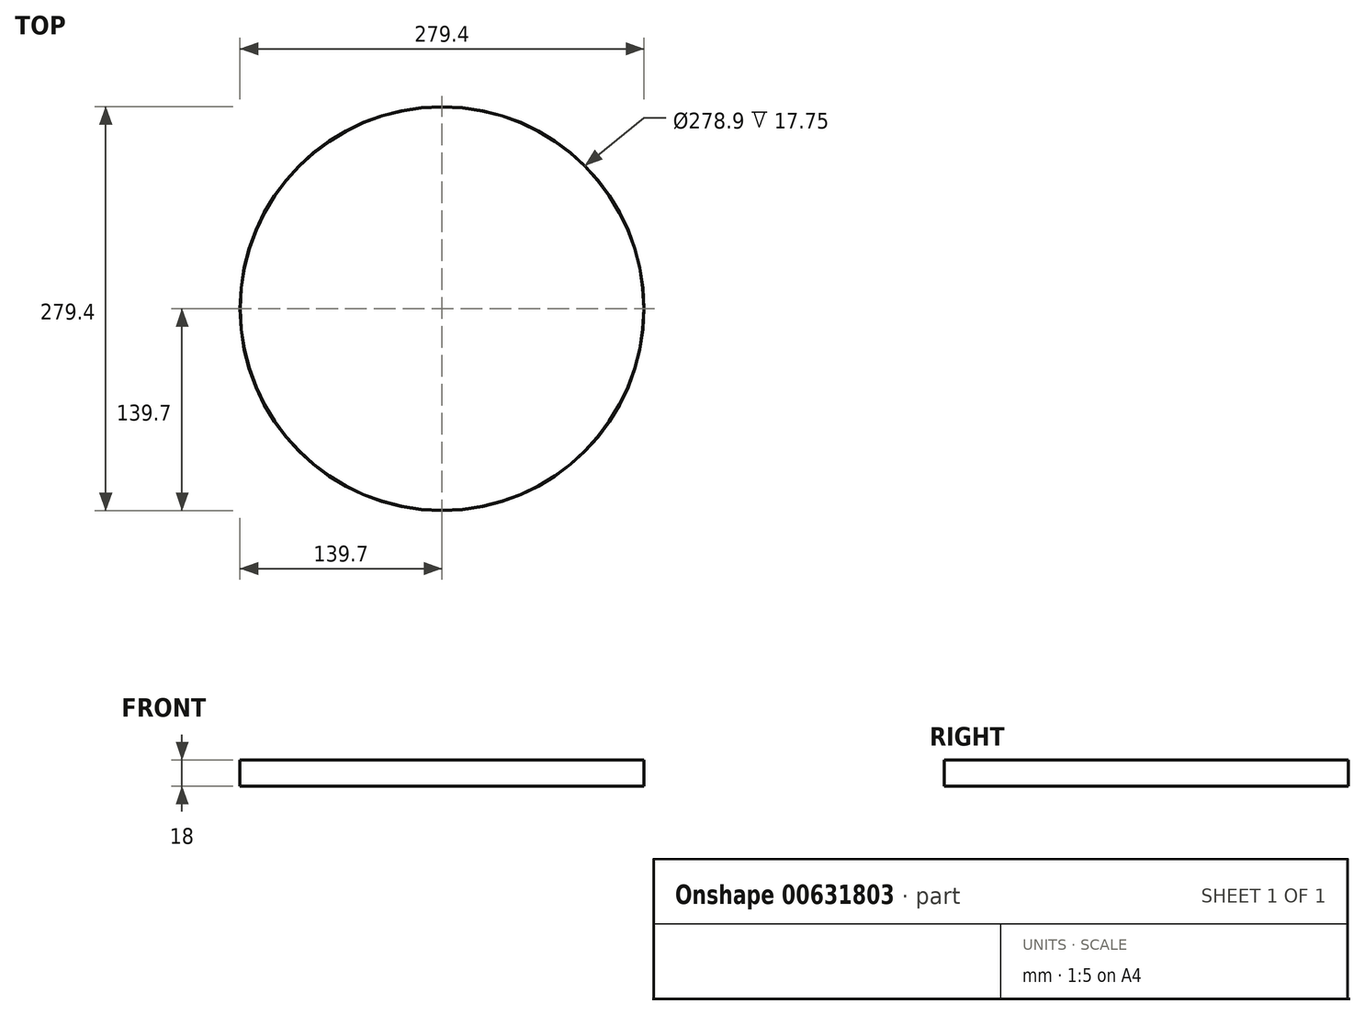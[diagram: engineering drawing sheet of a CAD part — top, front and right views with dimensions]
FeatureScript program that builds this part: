
annotation { "Feature Type Name" : "Feature", "Feature Type Description" : "" }
export const myFeature = defineFeature(function(context is Context, id is Id, definition is map)
    precondition{}
    {
        {
            assignVariable(context, id + "F0", {"name" : "epais", "anyValue" : .25});
        }
        {
            assignVariable(context, id + "F1", {"name" : "haut", "anyValue" : 18});
        }
        {
            var Q0;
            Q0=qCreatedBy(makeId("Top.planeOp"),FACE);
            var sketch = newSketch(context, id + "F2", { "sketchPlane" : qUnion([Q0])});
            skCircle(sketch, "E0", {"center": v(0, 0) * mm, "radius": 139.7 * mm});
            skSolve(sketch);
        }
        {
            var Q0;
            Q0 = qSketchRegion(id + "F2", true);
            extrude(context, id + "F3", {"entities" : qUnion([Q0]), "depth" : (getVariable(context, 'haut')) * mm, "offsetDistance" : 25.4 * mm});
        }
        {
            var Q0;
            Q0=makeQuery(id+"F3.opExtrude","CAP_FACE",FACE,{"disambiguationData":[OSD([sQuery(id+"F2.wireOp",EDGE,"E0")])],"isStart":false});
            shell(context, id + "F4", {"entities" : qUnion([Q0]), "thickness" : (getVariable(context, 'epais')) * mm});
        }
    });
